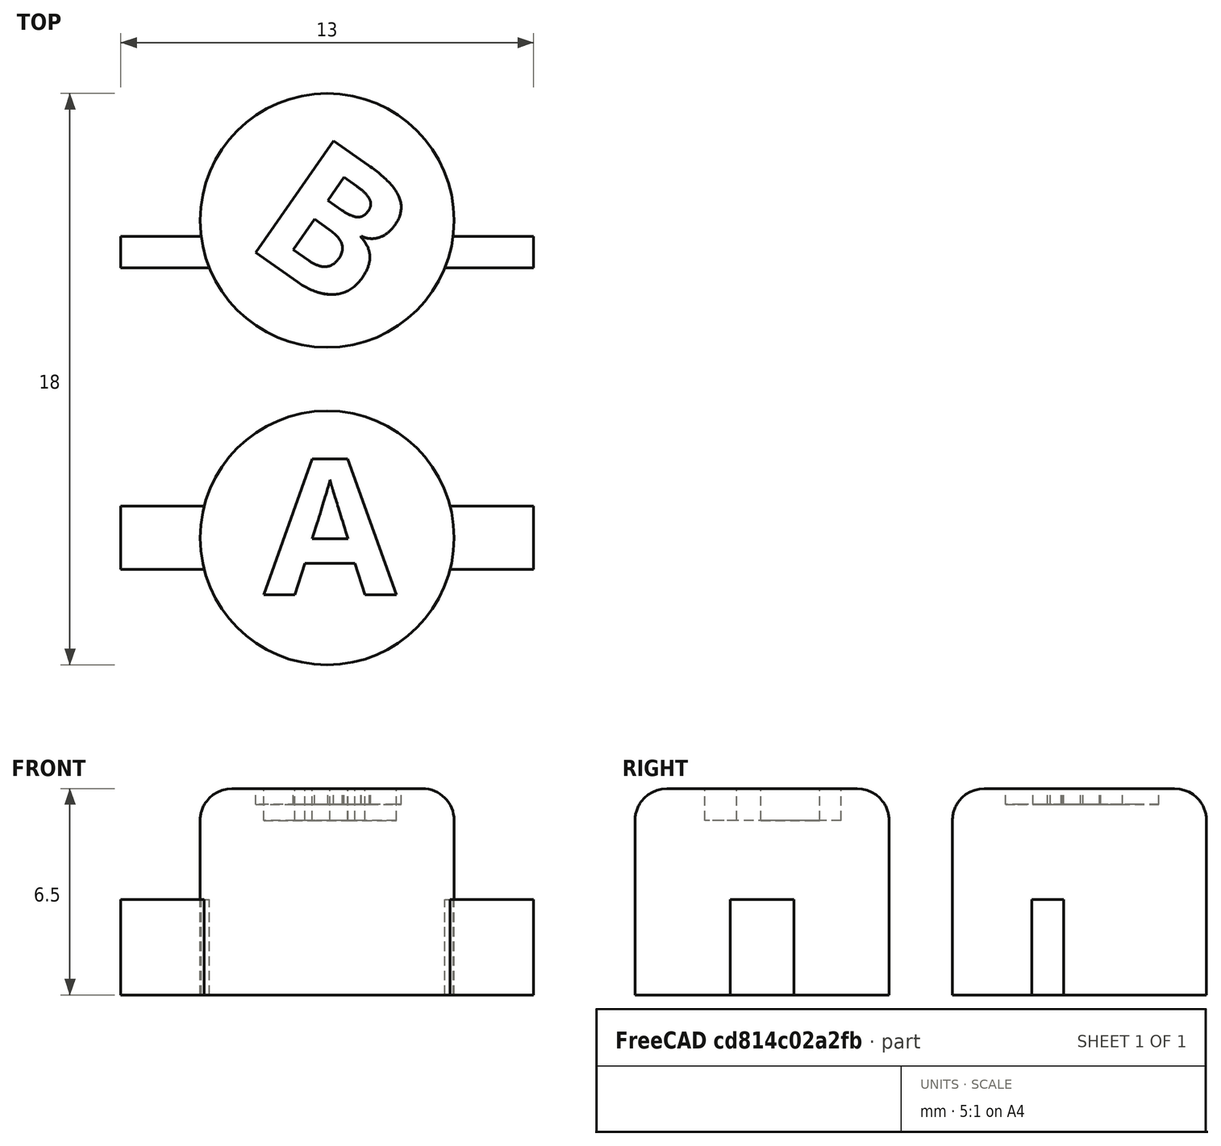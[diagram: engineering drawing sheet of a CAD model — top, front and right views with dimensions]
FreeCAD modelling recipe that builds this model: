
FCSTD DOCUMENT  (FreeCAD 0.18R16131 (Git))
Label: GBC_A_B
License: All rights reserved
LicenseURL: http://en.wikipedia.org/wiki/All_rights_reserved
objects: Part::Cylinder×2, Part::Box×2, Part::Fillet×2, Part::Part2DObjectPython×2, Part::Extrusion×2, Part::Cut×2, Part::MultiFuse×2
note: 14 computed .brp shape members not serialized (recipe doc carries the construction recipe); baked Part::Feature solids carry a one-line shape summary decoded from their .brp

FEATURE [Part::Cylinder] Cylinder
  Angle = 360
  AttacherType = Attacher::AttachEngine3D
  Height = 6.5
  Radius = 4
FEATURE [Part::Box] Box  label="Cube"
  AttacherType = Attacher::AttachEngine3D
  Height = 3
  Length = 13
  Placement = pos=(-6.5,-1,0) rot=(0,0,1;0rad)
  Width = 2
FEATURE [Part::Fillet] Fillet
  Base = -> Cylinder
  Edges = 1 edges r=1: [Edge1]
FEATURE [Part::Part2DObjectPython] ShapeString  # Draft 2D object (typed FeaturePython)
  FontFile = <userpath>/A6E4-ED97/3dprinting/fonts/open-sans/OpenSans-Bold.ttf
  Placement = pos=(-2,-2,7) rot=(0,0,1;0rad)
  Size = 5.5
  String = A
  Tracking = 0
FEATURE [Part::Part2DObjectPython] ShapeString001  # Draft 2D object (typed FeaturePython)
  FontFile = <userpath>/A6E4-ED97/3dprinting/fonts/open-sans/OpenSans-Bold.ttf
  Placement = pos=(-2.7,9.3,7) rot=(0,0,-1;0.610865rad)
  Size = 5.5
  String = B
  Tracking = 0
FEATURE [Part::Extrusion] Extrude
  Base = -> ShapeString
  Dir = (0,0,1)
  DirMode = 2
  FaceMakerClass = Part::FaceMakerBullseye
  LengthFwd = 1
  LengthRev = 0
  Placement = pos=(0,0.2,-1.5) rot=(0,0,1;0rad)
  Solid = false
  Symmetric = false
FEATURE [Part::Cylinder] Cylinder001
  Angle = 360
  AttacherType = Attacher::AttachEngine3D
  Height = 6.5
  Placement = pos=(0,10,0) rot=(0,0,1;0rad)
  Radius = 4
FEATURE [Part::Fillet] Fillet001
  Base = -> Cylinder001
  Edges = 1 edges r=1: [Edge1]
FEATURE [Part::Box] Box001  label="Cube001"
  AttacherType = Attacher::AttachEngine3D
  Height = 3
  Length = 13
  Placement = pos=(-6.5,8.5,0) rot=(0,0,1;0rad)
  Width = 1
FEATURE [Part::Extrusion] Extrude001
  Base = -> ShapeString001
  Dir = (0,0,1)
  DirMode = 2
  FaceMakerClass = Part::FaceMakerBullseye
  LengthFwd = 1
  LengthRev = 0
  Placement = pos=(0,0,-1) rot=(0,0,1;0rad)
  Solid = false
  Symmetric = false
FEATURE [Part::Cut] Cut
  Base = -> Fillet001
  Tool = -> Extrude001
FEATURE [Part::Cut] Cut001
  Base = -> Fillet
  Tool = -> Extrude
FEATURE [Part::MultiFuse] Fusion
  Shapes = -> [Cut001,Box]
FEATURE [Part::MultiFuse] Fusion001
  Shapes = -> [Cut,Box001]
